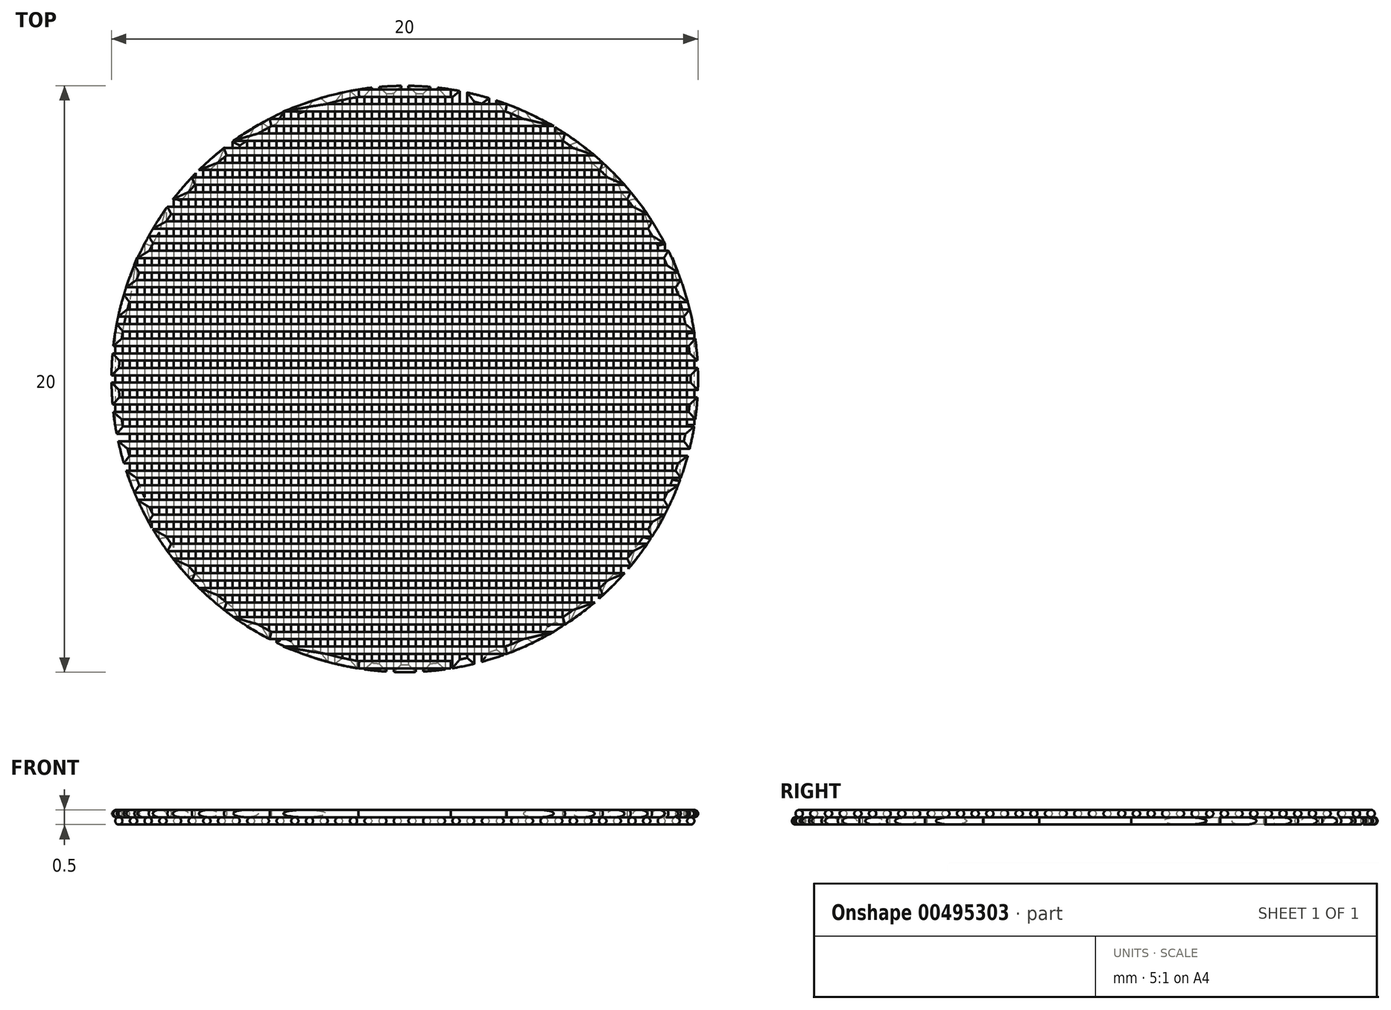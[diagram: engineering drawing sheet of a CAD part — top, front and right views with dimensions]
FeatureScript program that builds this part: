
annotation { "Feature Type Name" : "Feature", "Feature Type Description" : "" }
export const myFeature = defineFeature(function(context is Context, id is Id, definition is map)
    precondition{}
    {
        {
            assignVariable(context, id + "F0", {"name" : "d", "anyValue" : 0.25 * mm});
        }
        {
            var Q0;
            Q0=qCreatedBy(makeId("Top.planeOp"),FACE);
            cPlane(context, id + "F1", {"entities" : qUnion([Q0]), "cplaneType" : CPlaneType.OFFSET, "offset" : getVariable(context, 'd') / 2, "width" : 150 * mm, "height" : 150 * mm});
        }
        {
            var Q0;
            Q0=qCreatedBy(id+"F1.planeOp",FACE);
            var sketch = newSketch(context, id + "F2", { "sketchPlane" : qUnion([Q0])});
            skCircle(sketch, "E0", {"center": v(0, 0) * mm, "radius": 10 * mm, "construction": true});
            skCircle(sketch, "E1", {"center": v(0, 0) * mm, "radius": 9.88 * mm, "construction": true});
            skLineSegment(sketch, "E2", {"start": v(-9.88, 0) * mm, "end": v(-9.75, 0) * mm, "construction": true});
            skLineSegment(sketch, "E3", {"start": v(-9.75, 0) * mm, "end": v(-9.25, 0) * mm, "construction": true});
            skLineSegment(sketch, "E4", {"start": v(-9.25, 0) * mm, "end": v(-8.75, 0) * mm, "construction": true});
            skLineSegment(sketch, "E5", {"start": v(-8.75, 0) * mm, "end": v(-8.25, 0) * mm, "construction": true});
            skLineSegment(sketch, "E6", {"start": v(-8.25, 0) * mm, "end": v(-7.75, 0) * mm, "construction": true});
            skLineSegment(sketch, "E7", {"start": v(-7.75, 0) * mm, "end": v(-7.25, 0) * mm, "construction": true});
            skLineSegment(sketch, "E8", {"start": v(-7.25, 0) * mm, "end": v(-6.75, 0) * mm, "construction": true});
            skLineSegment(sketch, "E9", {"start": v(-6.75, 0) * mm, "end": v(-6.25, 0) * mm, "construction": true});
            skLineSegment(sketch, "E10", {"start": v(-6.25, 0) * mm, "end": v(-5.75, 0) * mm, "construction": true});
            skLineSegment(sketch, "E11", {"start": v(-5.75, 0) * mm, "end": v(-5.25, 0) * mm, "construction": true});
            skLineSegment(sketch, "E12", {"start": v(-5.25, 0) * mm, "end": v(-4.75, 0) * mm, "construction": true});
            skLineSegment(sketch, "E13", {"start": v(-4.75, 0) * mm, "end": v(-4.25, 0) * mm, "construction": true});
            skLineSegment(sketch, "E14", {"start": v(-4.25, 0) * mm, "end": v(-3.75, 0) * mm, "construction": true});
            skLineSegment(sketch, "E15", {"start": v(-3.75, 0) * mm, "end": v(-3.25, 0) * mm, "construction": true});
            skLineSegment(sketch, "E16", {"start": v(-3.25, 0) * mm, "end": v(-2.75, 0) * mm, "construction": true});
            skLineSegment(sketch, "E17", {"start": v(-2.75, 0) * mm, "end": v(-2.25, 0) * mm, "construction": true});
            skLineSegment(sketch, "E18", {"start": v(-2.25, 0) * mm, "end": v(-1.75, 0) * mm, "construction": true});
            skLineSegment(sketch, "E19", {"start": v(-1.75, 0) * mm, "end": v(-1.25, 0) * mm, "construction": true});
            skLineSegment(sketch, "E20", {"start": v(-1.25, 0) * mm, "end": v(-0.75, 0) * mm, "construction": true});
            skLineSegment(sketch, "E21", {"start": v(-0.75, 0) * mm, "end": v(-0.25, 0) * mm, "construction": true});
            skLineSegment(sketch, "E22", {"start": v(-0.25, 0) * mm, "end": v(0.25, 0) * mm, "construction": true});
            skLineSegment(sketch, "E23", {"start": v(0.25, 0) * mm, "end": v(0.75, 0) * mm, "construction": true});
            skLineSegment(sketch, "E24", {"start": v(0.75, 0) * mm, "end": v(1.25, 0) * mm, "construction": true});
            skLineSegment(sketch, "E25", {"start": v(1.25, 0) * mm, "end": v(1.75, 0) * mm, "construction": true});
            skLineSegment(sketch, "E26", {"start": v(1.75, 0) * mm, "end": v(2.25, 0) * mm, "construction": true});
            skLineSegment(sketch, "E27", {"start": v(2.25, 0) * mm, "end": v(2.75, 0) * mm, "construction": true});
            skLineSegment(sketch, "E28", {"start": v(2.75, 0) * mm, "end": v(3.25, 0) * mm, "construction": true});
            skLineSegment(sketch, "E29", {"start": v(3.25, 0) * mm, "end": v(3.75, 0) * mm, "construction": true});
            skLineSegment(sketch, "E30", {"start": v(3.75, 0) * mm, "end": v(4.25, 0) * mm, "construction": true});
            skLineSegment(sketch, "E31", {"start": v(4.25, 0) * mm, "end": v(4.75, 0) * mm, "construction": true});
            skLineSegment(sketch, "E32", {"start": v(4.75, 0) * mm, "end": v(5.25, 0) * mm, "construction": true});
            skLineSegment(sketch, "E33", {"start": v(5.25, 0) * mm, "end": v(5.75, 0) * mm, "construction": true});
            skLineSegment(sketch, "E34", {"start": v(5.75, 0) * mm, "end": v(6.25, 0) * mm, "construction": true});
            skLineSegment(sketch, "E35", {"start": v(6.25, 0) * mm, "end": v(6.75, 0) * mm, "construction": true});
            skLineSegment(sketch, "E36", {"start": v(6.75, 0) * mm, "end": v(7.25, 0) * mm, "construction": true});
            skLineSegment(sketch, "E37", {"start": v(7.25, 0) * mm, "end": v(7.75, 0) * mm, "construction": true});
            skLineSegment(sketch, "E38", {"start": v(7.75, 0) * mm, "end": v(8.25, 0) * mm, "construction": true});
            skLineSegment(sketch, "E39", {"start": v(8.25, 0) * mm, "end": v(8.75, 0) * mm, "construction": true});
            skLineSegment(sketch, "E40", {"start": v(8.75, 0) * mm, "end": v(9.25, 0) * mm, "construction": true});
            skLineSegment(sketch, "E41", {"start": v(9.25, 0) * mm, "end": v(9.75, 0) * mm, "construction": true});
            skLineSegment(sketch, "E42", {"start": v(9.75, 0) * mm, "end": v(9.88, 0) * mm, "construction": true});
            skLineSegment(sketch, "E43", {"start": v(0, 9.88) * mm, "end": v(0, 9.75) * mm, "construction": true});
            skLineSegment(sketch, "E44", {"start": v(0, 9.75) * mm, "end": v(0, 9.25) * mm, "construction": true});
            skLineSegment(sketch, "E45", {"start": v(0, 9.25) * mm, "end": v(0, 8.75) * mm, "construction": true});
            skLineSegment(sketch, "E46", {"start": v(0, 8.75) * mm, "end": v(0, 8.25) * mm, "construction": true});
            skLineSegment(sketch, "E47", {"start": v(0, 8.25) * mm, "end": v(0, 7.75) * mm, "construction": true});
            skLineSegment(sketch, "E48", {"start": v(0, 7.75) * mm, "end": v(0, 7.25) * mm, "construction": true});
            skLineSegment(sketch, "E49", {"start": v(0, 7.25) * mm, "end": v(0, 6.75) * mm, "construction": true});
            skLineSegment(sketch, "E50", {"start": v(0, 6.75) * mm, "end": v(0, 6.25) * mm, "construction": true});
            skLineSegment(sketch, "E51", {"start": v(0, 6.25) * mm, "end": v(0, 5.75) * mm, "construction": true});
            skLineSegment(sketch, "E52", {"start": v(0, 5.75) * mm, "end": v(0, 5.25) * mm, "construction": true});
            skLineSegment(sketch, "E53", {"start": v(0, 5.25) * mm, "end": v(0, 4.75) * mm, "construction": true});
            skLineSegment(sketch, "E54", {"start": v(0, 4.75) * mm, "end": v(0, 4.25) * mm, "construction": true});
            skLineSegment(sketch, "E55", {"start": v(0, 4.25) * mm, "end": v(0, 3.75) * mm, "construction": true});
            skLineSegment(sketch, "E56", {"start": v(0, 3.75) * mm, "end": v(0, 3.25) * mm, "construction": true});
            skLineSegment(sketch, "E57", {"start": v(0, 3.25) * mm, "end": v(0, 2.75) * mm, "construction": true});
            skLineSegment(sketch, "E58", {"start": v(0, 2.75) * mm, "end": v(0, 2.25) * mm, "construction": true});
            skLineSegment(sketch, "E59", {"start": v(0, 2.25) * mm, "end": v(0, 1.75) * mm, "construction": true});
            skLineSegment(sketch, "E60", {"start": v(0, 1.75) * mm, "end": v(0, 1.25) * mm, "construction": true});
            skLineSegment(sketch, "E61", {"start": v(0, 1.25) * mm, "end": v(0, 0.75) * mm, "construction": true});
            skLineSegment(sketch, "E62", {"start": v(0, 0.75) * mm, "end": v(0, 0.25) * mm, "construction": true});
            skLineSegment(sketch, "E63", {"start": v(0, 0.25) * mm, "end": v(0, -0.25) * mm, "construction": true});
            skLineSegment(sketch, "E64", {"start": v(0, -0.25) * mm, "end": v(0, -0.75) * mm, "construction": true});
            skLineSegment(sketch, "E65", {"start": v(0, -0.75) * mm, "end": v(0, -1.25) * mm, "construction": true});
            skLineSegment(sketch, "E66", {"start": v(0, -1.25) * mm, "end": v(0, -1.75) * mm, "construction": true});
            skLineSegment(sketch, "E67", {"start": v(0, -1.75) * mm, "end": v(0, -2.25) * mm, "construction": true});
            skLineSegment(sketch, "E68", {"start": v(0, -2.25) * mm, "end": v(0, -2.75) * mm, "construction": true});
            skLineSegment(sketch, "E69", {"start": v(0, -2.75) * mm, "end": v(0, -3.25) * mm, "construction": true});
            skLineSegment(sketch, "E70", {"start": v(0, -3.25) * mm, "end": v(0, -3.75) * mm, "construction": true});
            skLineSegment(sketch, "E71", {"start": v(0, -3.75) * mm, "end": v(0, -4.25) * mm, "construction": true});
            skLineSegment(sketch, "E72", {"start": v(0, -4.25) * mm, "end": v(0, -4.75) * mm, "construction": true});
            skLineSegment(sketch, "E73", {"start": v(0, -4.75) * mm, "end": v(0, -5.25) * mm, "construction": true});
            skLineSegment(sketch, "E74", {"start": v(0, -5.25) * mm, "end": v(0, -5.75) * mm, "construction": true});
            skLineSegment(sketch, "E75", {"start": v(0, -5.75) * mm, "end": v(0, -6.25) * mm, "construction": true});
            skLineSegment(sketch, "E76", {"start": v(0, -6.25) * mm, "end": v(0, -6.75) * mm, "construction": true});
            skLineSegment(sketch, "E77", {"start": v(0, -6.75) * mm, "end": v(0, -7.25) * mm, "construction": true});
            skLineSegment(sketch, "E78", {"start": v(0, -7.25) * mm, "end": v(0, -7.75) * mm, "construction": true});
            skLineSegment(sketch, "E79", {"start": v(0, -7.75) * mm, "end": v(0, -8.25) * mm, "construction": true});
            skLineSegment(sketch, "E80", {"start": v(0, -8.25) * mm, "end": v(0, -8.75) * mm, "construction": true});
            skLineSegment(sketch, "E81", {"start": v(0, -8.75) * mm, "end": v(0, -9.25) * mm, "construction": true});
            skLineSegment(sketch, "E82", {"start": v(0, -9.25) * mm, "end": v(0, -9.75) * mm, "construction": true});
            skLineSegment(sketch, "E83", {"start": v(0, -9.75) * mm, "end": v(0, -9.88) * mm, "construction": true});
            skLineSegment(sketch, "E84", {"start": v(-9.75, 1.57) * mm, "end": v(-9.75, -1.57) * mm});
            skLineSegment(sketch, "E85", {"start": v(-9.25, 3.46) * mm, "end": v(-9.25, -3.46) * mm});
            skLineSegment(sketch, "E86", {"start": v(-8.75, 4.58) * mm, "end": v(-8.75, -4.58) * mm});
            skLineSegment(sketch, "E87", {"start": v(-8.25, 5.43) * mm, "end": v(-8.25, -5.43) * mm});
            skLineSegment(sketch, "E88", {"start": v(-7.75, 6.12) * mm, "end": v(-7.75, -6.12) * mm});
            skLineSegment(sketch, "E89", {"start": v(-7.25, 6.7) * mm, "end": v(-7.25, -6.7) * mm});
            skLineSegment(sketch, "E90", {"start": v(-6.75, 7.2) * mm, "end": v(-6.75, -7.2) * mm});
            skLineSegment(sketch, "E91", {"start": v(-6.25, 7.65) * mm, "end": v(-6.25, -7.65) * mm});
            skLineSegment(sketch, "E92", {"start": v(-5.75, 8.03) * mm, "end": v(-5.75, -8.03) * mm});
            skLineSegment(sketch, "E93", {"start": v(-5.25, 8.36) * mm, "end": v(-5.25, -8.36) * mm});
            skLineSegment(sketch, "E94", {"start": v(-4.75, 8.66) * mm, "end": v(-4.75, -8.66) * mm});
            skLineSegment(sketch, "E95", {"start": v(-4.25, 8.91) * mm, "end": v(-4.25, -8.91) * mm});
            skLineSegment(sketch, "E96", {"start": v(-3.75, 9.14) * mm, "end": v(-3.75, -9.14) * mm});
            skLineSegment(sketch, "E97", {"start": v(-3.25, 9.32) * mm, "end": v(-3.25, -9.32) * mm});
            skLineSegment(sketch, "E98", {"start": v(-2.75, 9.48) * mm, "end": v(-2.75, -9.48) * mm});
            skLineSegment(sketch, "E99", {"start": v(-2.25, 9.62) * mm, "end": v(-2.25, -9.62) * mm});
            skLineSegment(sketch, "E100", {"start": v(-1.75, -9.72) * mm, "end": v(-1.75, 9.72) * mm});
            skLineSegment(sketch, "E101", {"start": v(-1.25, 9.8) * mm, "end": v(-1.25, -9.8) * mm});
            skLineSegment(sketch, "E102", {"start": v(-0.75, 9.85) * mm, "end": v(-0.75, -9.85) * mm});
            skLineSegment(sketch, "E103", {"start": v(-0.25, 9.87) * mm, "end": v(-0.25, -9.87) * mm});
            skLineSegment(sketch, "E104", {"start": v(0.25, -9.87) * mm, "end": v(0.25, 9.87) * mm});
            skLineSegment(sketch, "E105", {"start": v(0.75, 9.85) * mm, "end": v(0.75, -9.85) * mm});
            skLineSegment(sketch, "E106", {"start": v(1.25, -9.8) * mm, "end": v(1.25, 9.8) * mm});
            skLineSegment(sketch, "E107", {"start": v(1.75, 9.72) * mm, "end": v(1.75, -9.72) * mm});
            skLineSegment(sketch, "E108", {"start": v(2.25, 9.62) * mm, "end": v(2.25, -9.62) * mm});
            skLineSegment(sketch, "E109", {"start": v(2.75, 9.48) * mm, "end": v(2.75, -9.48) * mm});
            skLineSegment(sketch, "E110", {"start": v(3.25, 9.32) * mm, "end": v(3.25, -9.32) * mm});
            skLineSegment(sketch, "E111", {"start": v(3.75, 9.14) * mm, "end": v(3.75, -9.14) * mm});
            skLineSegment(sketch, "E112", {"start": v(4.25, 8.91) * mm, "end": v(4.25, -8.91) * mm});
            skLineSegment(sketch, "E113", {"start": v(4.75, 8.66) * mm, "end": v(4.75, -8.66) * mm});
            skLineSegment(sketch, "E114", {"start": v(5.25, 8.36) * mm, "end": v(5.25, -8.36) * mm});
            skLineSegment(sketch, "E115", {"start": v(5.75, 8.03) * mm, "end": v(5.75, -8.03) * mm});
            skLineSegment(sketch, "E116", {"start": v(6.25, 7.65) * mm, "end": v(6.25, -7.65) * mm});
            skLineSegment(sketch, "E117", {"start": v(6.75, -7.2) * mm, "end": v(6.75, 7.2) * mm});
            skLineSegment(sketch, "E118", {"start": v(7.25, -6.7) * mm, "end": v(7.25, 6.7) * mm});
            skLineSegment(sketch, "E119", {"start": v(7.75, -6.12) * mm, "end": v(7.75, 6.12) * mm});
            skLineSegment(sketch, "E120", {"start": v(8.25, -5.43) * mm, "end": v(8.25, 5.43) * mm});
            skLineSegment(sketch, "E121", {"start": v(8.75, -4.58) * mm, "end": v(8.75, 4.58) * mm});
            skLineSegment(sketch, "E122", {"start": v(9.25, -3.46) * mm, "end": v(9.25, 3.46) * mm});
            skLineSegment(sketch, "E123", {"start": v(9.75, -1.57) * mm, "end": v(9.75, 1.57) * mm});
            skArc(sketch, "E124", {"start": v(9.75, 1.57) * mm, "mid": v(9.55, 2.52) * mm, "end": v(9.25, 3.46) * mm});
            skArc(sketch, "E125", {"start": v(8.75, 4.58) * mm, "mid": v(8.51, 5) * mm, "end": v(8.25, 5.43) * mm});
            skArc(sketch, "E126", {"start": v(7.75, 6.12) * mm, "mid": v(7.5, 6.42) * mm, "end": v(7.25, 6.7) * mm});
            skArc(sketch, "E127", {"start": v(6.75, 7.2) * mm, "mid": v(6.5, 7.43) * mm, "end": v(6.25, 7.65) * mm});
            skArc(sketch, "E128", {"start": v(5.75, 8.03) * mm, "mid": v(5.5, 8.2) * mm, "end": v(5.25, 8.36) * mm});
            skArc(sketch, "E129", {"start": v(4.75, 8.66) * mm, "mid": v(4.5, 8.79) * mm, "end": v(4.25, 8.91) * mm});
            skArc(sketch, "E130", {"start": v(3.75, 9.14) * mm, "mid": v(3.5, 9.23) * mm, "end": v(3.25, 9.32) * mm});
            skArc(sketch, "E131", {"start": v(2.75, 9.48) * mm, "mid": v(2.5, 9.55) * mm, "end": v(2.25, 9.62) * mm});
            skArc(sketch, "E132", {"start": v(1.75, 9.72) * mm, "mid": v(1.5, 9.76) * mm, "end": v(1.25, 9.8) * mm});
            skArc(sketch, "E133", {"start": v(0.75, 9.85) * mm, "mid": v(0.5, 9.86) * mm, "end": v(0.25, 9.87) * mm});
            skArc(sketch, "E134", {"start": v(-0.25, 9.87) * mm, "mid": v(-0.5, 9.86) * mm, "end": v(-0.75, 9.85) * mm});
            skArc(sketch, "E135", {"start": v(-1.25, 9.8) * mm, "mid": v(-1.5, 9.76) * mm, "end": v(-1.75, 9.72) * mm});
            skArc(sketch, "E136", {"start": v(-2.25, 9.62) * mm, "mid": v(-2.5, 9.55) * mm, "end": v(-2.75, 9.48) * mm});
            skArc(sketch, "E137", {"start": v(-3.25, 9.32) * mm, "mid": v(-3.5, 9.23) * mm, "end": v(-3.75, 9.14) * mm});
            skArc(sketch, "E138", {"start": v(-4.25, 8.91) * mm, "mid": v(-4.5, 8.79) * mm, "end": v(-4.75, 8.66) * mm});
            skArc(sketch, "E139", {"start": v(-5.25, 8.36) * mm, "mid": v(-5.5, 8.2) * mm, "end": v(-5.75, 8.03) * mm});
            skArc(sketch, "E140", {"start": v(-6.25, 7.65) * mm, "mid": v(-6.5, 7.43) * mm, "end": v(-6.75, 7.2) * mm});
            skArc(sketch, "E141", {"start": v(-7.25, 6.7) * mm, "mid": v(-7.5, 6.42) * mm, "end": v(-7.75, 6.12) * mm});
            skArc(sketch, "E142", {"start": v(-8.25, 5.43) * mm, "mid": v(-8.51, 5) * mm, "end": v(-8.75, 4.58) * mm});
            skArc(sketch, "E143", {"start": v(-9.25, 3.46) * mm, "mid": v(-9.55, 2.52) * mm, "end": v(-9.75, 1.57) * mm});
            skArc(sketch, "E144", {"start": v(-9.25, -3.46) * mm, "mid": v(-9.02, -4.03) * mm, "end": v(-8.75, -4.58) * mm});
            skArc(sketch, "E145", {"start": v(-8.25, -5.43) * mm, "mid": v(-8, -5.78) * mm, "end": v(-7.75, -6.12) * mm});
            skArc(sketch, "E146", {"start": v(-7.25, -6.7) * mm, "mid": v(-7, -6.96) * mm, "end": v(-6.75, -7.2) * mm});
            skArc(sketch, "E147", {"start": v(-6.25, -7.65) * mm, "mid": v(-6, -7.84) * mm, "end": v(-5.75, -8.03) * mm});
            skArc(sketch, "E148", {"start": v(-5.25, -8.36) * mm, "mid": v(-5, -8.51) * mm, "end": v(-4.75, -8.66) * mm});
            skArc(sketch, "E149", {"start": v(-4.25, -8.91) * mm, "mid": v(-4, -9.03) * mm, "end": v(-3.75, -9.14) * mm});
            skArc(sketch, "E150", {"start": v(-3.25, -9.32) * mm, "mid": v(-3, -9.4) * mm, "end": v(-2.75, -9.48) * mm});
            skArc(sketch, "E151", {"start": v(-2.25, -9.62) * mm, "mid": v(-2, -9.67) * mm, "end": v(-1.75, -9.72) * mm});
            skArc(sketch, "E152", {"start": v(-1.25, -9.8) * mm, "mid": v(-1, -9.82) * mm, "end": v(-0.75, -9.85) * mm});
            skArc(sketch, "E153", {"start": v(-0.25, -9.87) * mm, "mid": v(0, -9.88) * mm, "end": v(0.25, -9.87) * mm});
            skArc(sketch, "E154", {"start": v(0.75, -9.85) * mm, "mid": v(1, -9.82) * mm, "end": v(1.25, -9.8) * mm});
            skArc(sketch, "E155", {"start": v(1.75, -9.72) * mm, "mid": v(2, -9.67) * mm, "end": v(2.25, -9.62) * mm});
            skArc(sketch, "E156", {"start": v(2.75, -9.48) * mm, "mid": v(3, -9.4) * mm, "end": v(3.25, -9.32) * mm});
            skArc(sketch, "E157", {"start": v(3.75, -9.14) * mm, "mid": v(4, -9.03) * mm, "end": v(4.25, -8.91) * mm});
            skArc(sketch, "E158", {"start": v(4.75, -8.66) * mm, "mid": v(5, -8.51) * mm, "end": v(5.25, -8.36) * mm});
            skArc(sketch, "E159", {"start": v(5.75, -8.03) * mm, "mid": v(6, -7.84) * mm, "end": v(6.25, -7.65) * mm});
            skArc(sketch, "E160", {"start": v(6.75, -7.2) * mm, "mid": v(7, -6.96) * mm, "end": v(7.25, -6.7) * mm});
            skArc(sketch, "E161", {"start": v(7.75, -6.12) * mm, "mid": v(8, -5.78) * mm, "end": v(8.25, -5.43) * mm});
            skArc(sketch, "E162", {"start": v(8.75, -4.58) * mm, "mid": v(9.02, -4.03) * mm, "end": v(9.25, -3.46) * mm});
            skSolve(sketch);
        }
        {
            var Q0;
            Q0=sQuery(id+"F2.wireOp",EDGE,"E123");
            var Q1;
            Q1=sQuery(id+"F2.wireOp",VERTEX,"E123.start");
            cPlane(context, id + "F3", {"entities" : qUnion([Q0, Q1]), "cplaneType" : CPlaneType.LINE_POINT, "offset" : 25 * mm, "width" : 150 * mm, "height" : 150 * mm});
        }
        {
            var Q0;
            Q0=qCreatedBy(id+"F3.planeOp",FACE);
            var sketch = newSketch(context, id + "F4", { "sketchPlane" : qUnion([Q0])});
            skCircle(sketch, "E163", {"center": v(-9.75, 0.12) * mm, "radius": 0.12 * mm});
            skSolve(sketch);
        }
        {
            var Q0;
            Q0=makeQuery(id+"F4.imprint","IMPRINT",FACE,{"disambiguationData":[TD([[makeQuery(id+"F4.imprint","IMPRINT",EDGE,{"derivedFrom":sQuery(id+"F4.wireOp",EDGE,"E163")}),1.0]])]});
            var Q1;
            Q1=sQuery(id+"F2.wireOp",EDGE,"E123");
            var Q2;
            Q2=sQuery(id+"F2.wireOp",EDGE,"E124");
            var Q3;
            Q3=sQuery(id+"F2.wireOp",EDGE,"E122");
            var Q4;
            Q4=sQuery(id+"F2.wireOp",EDGE,"E162");
            var Q5;
            Q5=sQuery(id+"F2.wireOp",EDGE,"E120");
            var Q6;
            Q6=sQuery(id+"F2.wireOp",EDGE,"E125");
            var Q7;
            Q7=sQuery(id+"F2.wireOp",EDGE,"E121");
            var Q8;
            Q8=sQuery(id+"F2.wireOp",EDGE,"E126");
            var Q9;
            Q9=sQuery(id+"F2.wireOp",EDGE,"E119");
            var Q10;
            Q10=sQuery(id+"F2.wireOp",EDGE,"E118");
            var Q11;
            Q11=sQuery(id+"F2.wireOp",EDGE,"E117");
            var Q12;
            Q12=sQuery(id+"F2.wireOp",EDGE,"E127");
            var Q13;
            Q13=sQuery(id+"F2.wireOp",EDGE,"E116");
            var Q14;
            Q14=sQuery(id+"F2.wireOp",EDGE,"E115");
            var Q15;
            Q15=sQuery(id+"F2.wireOp",EDGE,"E128");
            var Q16;
            Q16=sQuery(id+"F2.wireOp",EDGE,"E114");
            var Q17;
            Q17=sQuery(id+"F2.wireOp",EDGE,"E113");
            var Q18;
            Q18=sQuery(id+"F2.wireOp",EDGE,"E112");
            var Q19;
            Q19=sQuery(id+"F2.wireOp",EDGE,"E111");
            var Q20;
            Q20=sQuery(id+"F2.wireOp",EDGE,"E110");
            var Q21;
            Q21=sQuery(id+"F2.wireOp",EDGE,"E109");
            var Q22;
            Q22=sQuery(id+"F2.wireOp",EDGE,"E129");
            var Q23;
            Q23=sQuery(id+"F2.wireOp",EDGE,"E130");
            var Q24;
            Q24=sQuery(id+"F2.wireOp",EDGE,"E131");
            var Q25;
            Q25=sQuery(id+"F2.wireOp",EDGE,"E108");
            var Q26;
            Q26=sQuery(id+"F2.wireOp",EDGE,"E107");
            var Q27;
            Q27=sQuery(id+"F2.wireOp",EDGE,"E132");
            var Q28;
            Q28=sQuery(id+"F2.wireOp",EDGE,"E106");
            var Q29;
            Q29=sQuery(id+"F2.wireOp",EDGE,"E133");
            var Q30;
            Q30=sQuery(id+"F2.wireOp",EDGE,"E105");
            var Q31;
            Q31=sQuery(id+"F2.wireOp",EDGE,"E104");
            var Q32;
            Q32=sQuery(id+"F2.wireOp",EDGE,"E134");
            var Q33;
            Q33=sQuery(id+"F2.wireOp",EDGE,"E101");
            var Q34;
            Q34=sQuery(id+"F2.wireOp",EDGE,"E135");
            var Q35;
            Q35=sQuery(id+"F2.wireOp",EDGE,"E100");
            var Q36;
            Q36=sQuery(id+"F2.wireOp",EDGE,"E99");
            var Q37;
            Q37=sQuery(id+"F2.wireOp",EDGE,"E136");
            var Q38;
            Q38=sQuery(id+"F2.wireOp",EDGE,"E98");
            var Q39;
            Q39=sQuery(id+"F2.wireOp",EDGE,"E97");
            var Q40;
            Q40=sQuery(id+"F2.wireOp",EDGE,"E137");
            var Q41;
            Q41=sQuery(id+"F2.wireOp",EDGE,"E96");
            var Q42;
            Q42=sQuery(id+"F2.wireOp",EDGE,"E95");
            var Q43;
            Q43=sQuery(id+"F2.wireOp",EDGE,"E138");
            var Q44;
            Q44=sQuery(id+"F2.wireOp",EDGE,"E94");
            var Q45;
            Q45=sQuery(id+"F2.wireOp",EDGE,"E93");
            var Q46;
            Q46=sQuery(id+"F2.wireOp",EDGE,"E139");
            var Q47;
            Q47=sQuery(id+"F2.wireOp",EDGE,"E92");
            var Q48;
            Q48=sQuery(id+"F2.wireOp",EDGE,"E91");
            var Q49;
            Q49=sQuery(id+"F2.wireOp",EDGE,"E140");
            var Q50;
            Q50=sQuery(id+"F2.wireOp",EDGE,"E90");
            var Q51;
            Q51=sQuery(id+"F2.wireOp",EDGE,"E89");
            var Q52;
            Q52=sQuery(id+"F2.wireOp",EDGE,"E141");
            var Q53;
            Q53=sQuery(id+"F2.wireOp",EDGE,"E88");
            var Q54;
            Q54=sQuery(id+"F2.wireOp",EDGE,"E102");
            var Q55;
            Q55=sQuery(id+"F2.wireOp",EDGE,"E103");
            var Q56;
            Q56=sQuery(id+"F2.wireOp",EDGE,"E87");
            var Q57;
            Q57=sQuery(id+"F2.wireOp",EDGE,"E142");
            var Q58;
            Q58=sQuery(id+"F2.wireOp",EDGE,"E86");
            var Q59;
            Q59=sQuery(id+"F2.wireOp",EDGE,"E85");
            var Q60;
            Q60=sQuery(id+"F2.wireOp",EDGE,"E143");
            var Q61;
            Q61=sQuery(id+"F2.wireOp",EDGE,"E84");
            var Q62;
            Q62=sQuery(id+"F2.wireOp",EDGE,"E144");
            var Q63;
            Q63=sQuery(id+"F2.wireOp",EDGE,"E145");
            var Q64;
            Q64=sQuery(id+"F2.wireOp",EDGE,"E146");
            var Q65;
            Q65=sQuery(id+"F2.wireOp",EDGE,"E147");
            var Q66;
            Q66=sQuery(id+"F2.wireOp",EDGE,"E148");
            var Q67;
            Q67=sQuery(id+"F2.wireOp",EDGE,"E149");
            var Q68;
            Q68=sQuery(id+"F2.wireOp",EDGE,"E150");
            var Q69;
            Q69=sQuery(id+"F2.wireOp",EDGE,"E151");
            var Q70;
            Q70=sQuery(id+"F2.wireOp",EDGE,"E152");
            var Q71;
            Q71=sQuery(id+"F2.wireOp",EDGE,"E153");
            var Q72;
            Q72=sQuery(id+"F2.wireOp",EDGE,"E154");
            var Q73;
            Q73=sQuery(id+"F2.wireOp",EDGE,"E155");
            var Q74;
            Q74=sQuery(id+"F2.wireOp",EDGE,"E156");
            var Q75;
            Q75=sQuery(id+"F2.wireOp",EDGE,"E157");
            var Q76;
            Q76=sQuery(id+"F2.wireOp",EDGE,"E158");
            var Q77;
            Q77=sQuery(id+"F2.wireOp",EDGE,"E159");
            var Q78;
            Q78=sQuery(id+"F2.wireOp",EDGE,"E160");
            var Q79;
            Q79=sQuery(id+"F2.wireOp",EDGE,"E161");
            var Q80;
            Q80=sQuery(id+"F2.wireOp",EDGE,"E146");
            var Q81;
            Q81=sQuery(id+"F2.wireOp",EDGE,"E147");
            var Q82;
            Q82=sQuery(id+"F2.wireOp",EDGE,"E157");
            sweep(context, id + "F5", {"profiles" : qUnion([Q0]), "path" : qUnion([Q1, Q2, Q3, Q4, Q5, Q6, Q7, Q8, Q9, Q10, Q11, Q12, Q13, Q14, Q15, Q16, Q17, Q18, Q19, Q20, Q21, Q22, Q23, Q24, Q25, Q26, Q27, Q28, Q29, Q30, Q31, Q32, Q33, Q34, Q35, Q36, Q37, Q38, Q39, Q40, Q41, Q42, Q43, Q44, Q45, Q46, Q47, Q48, Q49, Q50, Q51, Q52, Q53, Q54, Q55, Q56, Q57, Q58, Q59, Q60, Q61, Q62, Q63, Q64, Q65, Q66, Q67, Q68, Q69, Q70, Q71, Q72, Q73, Q74, Q75, Q76, Q77, Q78, Q79, Q80, Q81, Q82])});
        }
        {
            var Q0;
            Q0=qCreatedBy(id+"F1.planeOp",FACE);
            cPlane(context, id + "F6", {"entities" : qUnion([Q0]), "cplaneType" : CPlaneType.OFFSET, "offset" : getVariable(context, 'd'), "width" : 150 * mm, "height" : 150 * mm});
        }
        {
            var Q0;
            Q0=qCreatedBy(id+"F6.planeOp",FACE);
            var sketch = newSketch(context, id + "F7", { "sketchPlane" : qUnion([Q0])});
            skCircle(sketch, "E164", {"center": v(0, 0) * mm, "radius": 10 * mm, "construction": true});
            skCircle(sketch, "E165", {"center": v(0, 0) * mm, "radius": 9.88 * mm, "construction": true});
            skLineSegment(sketch, "E166", {"start": v(0, -9.88) * mm, "end": v(0, -9.75) * mm, "construction": true});
            skLineSegment(sketch, "E167", {"start": v(0, -9.75) * mm, "end": v(0, -9.25) * mm, "construction": true});
            skLineSegment(sketch, "E168", {"start": v(0, -9.25) * mm, "end": v(0, -8.75) * mm, "construction": true});
            skLineSegment(sketch, "E169", {"start": v(0, -8.75) * mm, "end": v(0, -8.25) * mm, "construction": true});
            skLineSegment(sketch, "E170", {"start": v(0, -8.25) * mm, "end": v(0, -7.75) * mm, "construction": true});
            skLineSegment(sketch, "E171", {"start": v(0, -7.75) * mm, "end": v(0, -7.25) * mm, "construction": true});
            skLineSegment(sketch, "E172", {"start": v(0, -7.25) * mm, "end": v(0, -6.75) * mm, "construction": true});
            skLineSegment(sketch, "E173", {"start": v(0, -6.75) * mm, "end": v(0, -6.25) * mm, "construction": true});
            skLineSegment(sketch, "E174", {"start": v(0, -6.25) * mm, "end": v(0, -5.75) * mm, "construction": true});
            skLineSegment(sketch, "E175", {"start": v(0, -5.75) * mm, "end": v(0, -5.25) * mm, "construction": true});
            skLineSegment(sketch, "E176", {"start": v(0, -5.25) * mm, "end": v(0, -4.75) * mm, "construction": true});
            skLineSegment(sketch, "E177", {"start": v(0, -4.75) * mm, "end": v(0, -4.25) * mm, "construction": true});
            skLineSegment(sketch, "E178", {"start": v(0, -4.25) * mm, "end": v(0, -3.75) * mm, "construction": true});
            skLineSegment(sketch, "E179", {"start": v(0, -3.75) * mm, "end": v(0, -3.25) * mm, "construction": true});
            skLineSegment(sketch, "E180", {"start": v(0, -3.25) * mm, "end": v(0, -2.75) * mm, "construction": true});
            skLineSegment(sketch, "E181", {"start": v(0, -2.75) * mm, "end": v(0, -2.25) * mm, "construction": true});
            skLineSegment(sketch, "E182", {"start": v(0, -2.25) * mm, "end": v(0, -1.75) * mm, "construction": true});
            skLineSegment(sketch, "E183", {"start": v(0, -1.75) * mm, "end": v(0, -1.25) * mm, "construction": true});
            skLineSegment(sketch, "E184", {"start": v(0, -1.25) * mm, "end": v(0, -0.75) * mm, "construction": true});
            skLineSegment(sketch, "E185", {"start": v(0, -0.75) * mm, "end": v(0, -0.25) * mm, "construction": true});
            skLineSegment(sketch, "E186", {"start": v(0, -0.25) * mm, "end": v(0, 0.25) * mm, "construction": true});
            skLineSegment(sketch, "E187", {"start": v(0, 0.25) * mm, "end": v(0, 0.75) * mm, "construction": true});
            skLineSegment(sketch, "E188", {"start": v(0, 0.75) * mm, "end": v(0, 1.25) * mm, "construction": true});
            skLineSegment(sketch, "E189", {"start": v(0, 1.25) * mm, "end": v(0, 1.75) * mm, "construction": true});
            skLineSegment(sketch, "E190", {"start": v(0, 1.75) * mm, "end": v(0, 2.25) * mm, "construction": true});
            skLineSegment(sketch, "E191", {"start": v(0, 2.25) * mm, "end": v(0, 2.75) * mm, "construction": true});
            skLineSegment(sketch, "E192", {"start": v(0, 2.75) * mm, "end": v(0, 3.25) * mm, "construction": true});
            skLineSegment(sketch, "E193", {"start": v(0, 3.25) * mm, "end": v(0, 3.75) * mm, "construction": true});
            skLineSegment(sketch, "E194", {"start": v(0, 3.75) * mm, "end": v(0, 4.25) * mm, "construction": true});
            skLineSegment(sketch, "E195", {"start": v(0, 4.25) * mm, "end": v(0, 4.75) * mm, "construction": true});
            skLineSegment(sketch, "E196", {"start": v(0, 4.75) * mm, "end": v(0, 5.25) * mm, "construction": true});
            skLineSegment(sketch, "E197", {"start": v(0, 5.25) * mm, "end": v(0, 5.75) * mm, "construction": true});
            skLineSegment(sketch, "E198", {"start": v(0, 5.75) * mm, "end": v(0, 6.25) * mm, "construction": true});
            skLineSegment(sketch, "E199", {"start": v(0, 6.25) * mm, "end": v(0, 6.75) * mm, "construction": true});
            skLineSegment(sketch, "E200", {"start": v(0, 6.75) * mm, "end": v(0, 7.25) * mm, "construction": true});
            skLineSegment(sketch, "E201", {"start": v(0, 7.25) * mm, "end": v(0, 7.75) * mm, "construction": true});
            skLineSegment(sketch, "E202", {"start": v(0, 7.75) * mm, "end": v(0, 8.25) * mm, "construction": true});
            skLineSegment(sketch, "E203", {"start": v(0, 8.25) * mm, "end": v(0, 8.75) * mm, "construction": true});
            skLineSegment(sketch, "E204", {"start": v(0, 8.75) * mm, "end": v(0, 9.25) * mm, "construction": true});
            skLineSegment(sketch, "E205", {"start": v(0, 9.25) * mm, "end": v(0, 9.75) * mm, "construction": true});
            skLineSegment(sketch, "E206", {"start": v(0, 9.75) * mm, "end": v(0, 9.88) * mm, "construction": true});
            skLineSegment(sketch, "E207", {"start": v(-1.57, -9.75) * mm, "end": v(1.57, -9.75) * mm});
            skLineSegment(sketch, "E208", {"start": v(-3.46, -9.25) * mm, "end": v(3.46, -9.25) * mm});
            skLineSegment(sketch, "E209", {"start": v(-4.58, -8.75) * mm, "end": v(4.58, -8.75) * mm});
            skLineSegment(sketch, "E210", {"start": v(-5.43, -8.25) * mm, "end": v(5.43, -8.25) * mm});
            skLineSegment(sketch, "E211", {"start": v(-6.12, -7.75) * mm, "end": v(6.12, -7.75) * mm});
            skLineSegment(sketch, "E212", {"start": v(-6.7, -7.25) * mm, "end": v(6.7, -7.25) * mm});
            skLineSegment(sketch, "E213", {"start": v(-7.2, -6.75) * mm, "end": v(7.2, -6.75) * mm});
            skLineSegment(sketch, "E214", {"start": v(-7.65, -6.25) * mm, "end": v(7.65, -6.25) * mm});
            skLineSegment(sketch, "E215", {"start": v(-8.03, -5.75) * mm, "end": v(8.03, -5.75) * mm});
            skLineSegment(sketch, "E216", {"start": v(-8.36, -5.25) * mm, "end": v(8.36, -5.25) * mm});
            skLineSegment(sketch, "E217", {"start": v(-8.66, -4.75) * mm, "end": v(8.66, -4.75) * mm});
            skLineSegment(sketch, "E218", {"start": v(-8.91, -4.25) * mm, "end": v(8.91, -4.25) * mm});
            skLineSegment(sketch, "E219", {"start": v(-9.14, -3.75) * mm, "end": v(9.14, -3.75) * mm});
            skLineSegment(sketch, "E220", {"start": v(-9.32, -3.25) * mm, "end": v(9.32, -3.25) * mm});
            skLineSegment(sketch, "E221", {"start": v(-9.48, -2.75) * mm, "end": v(9.48, -2.75) * mm});
            skLineSegment(sketch, "E222", {"start": v(-9.62, -2.25) * mm, "end": v(9.62, -2.25) * mm});
            skLineSegment(sketch, "E223", {"start": v(9.72, -1.75) * mm, "end": v(-9.72, -1.75) * mm});
            skLineSegment(sketch, "E224", {"start": v(-9.8, -1.25) * mm, "end": v(9.8, -1.25) * mm});
            skLineSegment(sketch, "E225", {"start": v(-9.85, -0.75) * mm, "end": v(9.85, -0.75) * mm});
            skLineSegment(sketch, "E226", {"start": v(-9.87, -0.25) * mm, "end": v(9.87, -0.25) * mm});
            skLineSegment(sketch, "E227", {"start": v(9.87, 0.25) * mm, "end": v(-9.87, 0.25) * mm});
            skLineSegment(sketch, "E228", {"start": v(-9.85, 0.75) * mm, "end": v(9.85, 0.75) * mm});
            skLineSegment(sketch, "E229", {"start": v(9.8, 1.25) * mm, "end": v(-9.8, 1.25) * mm});
            skLineSegment(sketch, "E230", {"start": v(-9.72, 1.75) * mm, "end": v(9.72, 1.75) * mm});
            skLineSegment(sketch, "E231", {"start": v(-9.62, 2.25) * mm, "end": v(9.62, 2.25) * mm});
            skLineSegment(sketch, "E232", {"start": v(-9.48, 2.75) * mm, "end": v(9.48, 2.75) * mm});
            skLineSegment(sketch, "E233", {"start": v(-9.32, 3.25) * mm, "end": v(9.32, 3.25) * mm});
            skLineSegment(sketch, "E234", {"start": v(-9.14, 3.75) * mm, "end": v(9.14, 3.75) * mm});
            skLineSegment(sketch, "E235", {"start": v(-8.91, 4.25) * mm, "end": v(8.91, 4.25) * mm});
            skLineSegment(sketch, "E236", {"start": v(-8.66, 4.75) * mm, "end": v(8.66, 4.75) * mm});
            skLineSegment(sketch, "E237", {"start": v(-8.36, 5.25) * mm, "end": v(8.36, 5.25) * mm});
            skLineSegment(sketch, "E238", {"start": v(-8.03, 5.75) * mm, "end": v(8.03, 5.75) * mm});
            skLineSegment(sketch, "E239", {"start": v(-7.65, 6.25) * mm, "end": v(7.65, 6.25) * mm});
            skLineSegment(sketch, "E240", {"start": v(7.2, 6.75) * mm, "end": v(-7.2, 6.75) * mm});
            skLineSegment(sketch, "E241", {"start": v(6.7, 7.25) * mm, "end": v(-6.7, 7.25) * mm});
            skLineSegment(sketch, "E242", {"start": v(6.12, 7.75) * mm, "end": v(-6.12, 7.75) * mm});
            skLineSegment(sketch, "E243", {"start": v(5.43, 8.25) * mm, "end": v(-5.43, 8.25) * mm});
            skLineSegment(sketch, "E244", {"start": v(4.58, 8.75) * mm, "end": v(-4.58, 8.75) * mm});
            skLineSegment(sketch, "E245", {"start": v(3.46, 9.25) * mm, "end": v(-3.46, 9.25) * mm});
            skLineSegment(sketch, "E246", {"start": v(1.57, 9.75) * mm, "end": v(-1.57, 9.75) * mm});
            skArc(sketch, "E247", {"start": v(-1.57, 9.75) * mm, "mid": v(-2.52, 9.55) * mm, "end": v(-3.46, 9.25) * mm});
            skArc(sketch, "E248", {"start": v(-4.58, 8.75) * mm, "mid": v(-5, 8.51) * mm, "end": v(-5.43, 8.25) * mm});
            skArc(sketch, "E249", {"start": v(-6.12, 7.75) * mm, "mid": v(-6.42, 7.5) * mm, "end": v(-6.7, 7.25) * mm});
            skArc(sketch, "E250", {"start": v(-7.2, 6.75) * mm, "mid": v(-7.43, 6.5) * mm, "end": v(-7.65, 6.25) * mm});
            skArc(sketch, "E251", {"start": v(-8.03, 5.75) * mm, "mid": v(-8.2, 5.5) * mm, "end": v(-8.36, 5.25) * mm});
            skArc(sketch, "E252", {"start": v(-8.66, 4.75) * mm, "mid": v(-8.79, 4.5) * mm, "end": v(-8.91, 4.25) * mm});
            skArc(sketch, "E253", {"start": v(-9.14, 3.75) * mm, "mid": v(-9.23, 3.5) * mm, "end": v(-9.32, 3.25) * mm});
            skArc(sketch, "E254", {"start": v(-9.48, 2.75) * mm, "mid": v(-9.55, 2.5) * mm, "end": v(-9.62, 2.25) * mm});
            skArc(sketch, "E255", {"start": v(-9.72, 1.75) * mm, "mid": v(-9.76, 1.5) * mm, "end": v(-9.8, 1.25) * mm});
            skArc(sketch, "E256", {"start": v(-9.85, 0.75) * mm, "mid": v(-9.86, 0.5) * mm, "end": v(-9.87, 0.25) * mm});
            skArc(sketch, "E257", {"start": v(-9.87, -0.25) * mm, "mid": v(-9.86, -0.5) * mm, "end": v(-9.85, -0.75) * mm});
            skArc(sketch, "E258", {"start": v(-9.8, -1.25) * mm, "mid": v(-9.76, -1.5) * mm, "end": v(-9.72, -1.75) * mm});
            skArc(sketch, "E259", {"start": v(-9.62, -2.25) * mm, "mid": v(-9.55, -2.5) * mm, "end": v(-9.48, -2.75) * mm});
            skArc(sketch, "E260", {"start": v(-9.32, -3.25) * mm, "mid": v(-9.23, -3.5) * mm, "end": v(-9.14, -3.75) * mm});
            skArc(sketch, "E261", {"start": v(-8.91, -4.25) * mm, "mid": v(-8.79, -4.5) * mm, "end": v(-8.66, -4.75) * mm});
            skArc(sketch, "E262", {"start": v(-8.36, -5.25) * mm, "mid": v(-8.2, -5.5) * mm, "end": v(-8.03, -5.75) * mm});
            skArc(sketch, "E263", {"start": v(-7.65, -6.25) * mm, "mid": v(-7.43, -6.5) * mm, "end": v(-7.2, -6.75) * mm});
            skArc(sketch, "E264", {"start": v(-6.7, -7.25) * mm, "mid": v(-6.42, -7.5) * mm, "end": v(-6.12, -7.75) * mm});
            skArc(sketch, "E265", {"start": v(-5.43, -8.25) * mm, "mid": v(-5, -8.51) * mm, "end": v(-4.58, -8.75) * mm});
            skArc(sketch, "E266", {"start": v(-3.46, -9.25) * mm, "mid": v(-2.52, -9.55) * mm, "end": v(-1.57, -9.75) * mm});
            skArc(sketch, "E267", {"start": v(3.46, -9.25) * mm, "mid": v(4.03, -9.02) * mm, "end": v(4.58, -8.75) * mm});
            skArc(sketch, "E268", {"start": v(5.43, -8.25) * mm, "mid": v(5.78, -8) * mm, "end": v(6.12, -7.75) * mm});
            skArc(sketch, "E269", {"start": v(6.7, -7.25) * mm, "mid": v(6.96, -7) * mm, "end": v(7.2, -6.75) * mm});
            skArc(sketch, "E270", {"start": v(7.65, -6.25) * mm, "mid": v(7.84, -6) * mm, "end": v(8.03, -5.75) * mm});
            skArc(sketch, "E271", {"start": v(8.36, -5.25) * mm, "mid": v(8.51, -5) * mm, "end": v(8.66, -4.75) * mm});
            skArc(sketch, "E272", {"start": v(8.91, -4.25) * mm, "mid": v(9.03, -4) * mm, "end": v(9.14, -3.75) * mm});
            skArc(sketch, "E273", {"start": v(9.32, -3.25) * mm, "mid": v(9.4, -3) * mm, "end": v(9.48, -2.75) * mm});
            skArc(sketch, "E274", {"start": v(9.62, -2.25) * mm, "mid": v(9.67, -2) * mm, "end": v(9.72, -1.75) * mm});
            skArc(sketch, "E275", {"start": v(9.8, -1.25) * mm, "mid": v(9.82, -1) * mm, "end": v(9.85, -0.75) * mm});
            skArc(sketch, "E276", {"start": v(9.87, -0.25) * mm, "mid": v(9.88, 0) * mm, "end": v(9.87, 0.25) * mm});
            skArc(sketch, "E277", {"start": v(9.85, 0.75) * mm, "mid": v(9.82, 1) * mm, "end": v(9.8, 1.25) * mm});
            skArc(sketch, "E278", {"start": v(9.72, 1.75) * mm, "mid": v(9.67, 2) * mm, "end": v(9.62, 2.25) * mm});
            skArc(sketch, "E279", {"start": v(9.48, 2.75) * mm, "mid": v(9.4, 3) * mm, "end": v(9.32, 3.25) * mm});
            skArc(sketch, "E280", {"start": v(9.14, 3.75) * mm, "mid": v(9.03, 4) * mm, "end": v(8.91, 4.25) * mm});
            skArc(sketch, "E281", {"start": v(8.66, 4.75) * mm, "mid": v(8.51, 5) * mm, "end": v(8.36, 5.25) * mm});
            skArc(sketch, "E282", {"start": v(8.03, 5.75) * mm, "mid": v(7.84, 6) * mm, "end": v(7.65, 6.25) * mm});
            skArc(sketch, "E283", {"start": v(7.2, 6.75) * mm, "mid": v(6.96, 7) * mm, "end": v(6.7, 7.25) * mm});
            skArc(sketch, "E284", {"start": v(6.12, 7.75) * mm, "mid": v(5.78, 8) * mm, "end": v(5.43, 8.25) * mm});
            skArc(sketch, "E285", {"start": v(4.58, 8.75) * mm, "mid": v(4.03, 9.02) * mm, "end": v(3.46, 9.25) * mm});
            skSolve(sketch);
        }
        {
            var Q0;
            Q0=sQuery(id+"F7.wireOp",EDGE,"E246");
            var Q1;
            Q1=sQuery(id+"F7.wireOp",VERTEX,"E246.start");
            cPlane(context, id + "F8", {"entities" : qUnion([Q0, Q1]), "cplaneType" : CPlaneType.LINE_POINT, "offset" : 25 * mm, "width" : 150 * mm, "height" : 150 * mm});
        }
        {
            var Q0;
            Q0=qCreatedBy(id+"F8.planeOp",FACE);
            var sketch = newSketch(context, id + "F9", { "sketchPlane" : qUnion([Q0])});
            skCircle(sketch, "E286", {"center": v(-9.75, 0.38) * mm, "radius": 0.12 * mm});
            skSolve(sketch);
        }
        {
            var Q0;
            Q0=makeQuery(id+"F9.imprint","IMPRINT",FACE,{"disambiguationData":[TD([[makeQuery(id+"F9.imprint","IMPRINT",EDGE,{"derivedFrom":sQuery(id+"F9.wireOp",EDGE,"E286")}),1.0]])]});
            var Q1;
            Q1=sQuery(id+"F7.wireOp",EDGE,"E246");
            var Q2;
            Q2=sQuery(id+"F7.wireOp",EDGE,"E247");
            var Q3;
            Q3=sQuery(id+"F7.wireOp",EDGE,"E245");
            var Q4;
            Q4=sQuery(id+"F7.wireOp",EDGE,"E244");
            var Q5;
            Q5=sQuery(id+"F7.wireOp",EDGE,"E243");
            var Q6;
            Q6=sQuery(id+"F7.wireOp",EDGE,"E242");
            var Q7;
            Q7=sQuery(id+"F7.wireOp",EDGE,"E241");
            var Q8;
            Q8=sQuery(id+"F7.wireOp",EDGE,"E240");
            var Q9;
            Q9=sQuery(id+"F7.wireOp",EDGE,"E239");
            var Q10;
            Q10=sQuery(id+"F7.wireOp",EDGE,"E238");
            var Q11;
            Q11=sQuery(id+"F7.wireOp",EDGE,"E237");
            var Q12;
            Q12=sQuery(id+"F7.wireOp",EDGE,"E236");
            var Q13;
            Q13=sQuery(id+"F7.wireOp",EDGE,"E235");
            var Q14;
            Q14=sQuery(id+"F7.wireOp",EDGE,"E234");
            var Q15;
            Q15=sQuery(id+"F7.wireOp",EDGE,"E233");
            var Q16;
            Q16=sQuery(id+"F7.wireOp",EDGE,"E232");
            var Q17;
            Q17=sQuery(id+"F7.wireOp",EDGE,"E231");
            var Q18;
            Q18=sQuery(id+"F7.wireOp",EDGE,"E230");
            var Q19;
            Q19=sQuery(id+"F7.wireOp",EDGE,"E229");
            var Q20;
            Q20=sQuery(id+"F7.wireOp",EDGE,"E228");
            var Q21;
            Q21=sQuery(id+"F7.wireOp",EDGE,"E227");
            var Q22;
            Q22=sQuery(id+"F7.wireOp",EDGE,"E226");
            var Q23;
            Q23=sQuery(id+"F7.wireOp",EDGE,"E225");
            var Q24;
            Q24=sQuery(id+"F7.wireOp",EDGE,"E224");
            var Q25;
            Q25=sQuery(id+"F7.wireOp",EDGE,"E223");
            var Q26;
            Q26=sQuery(id+"F7.wireOp",EDGE,"E222");
            var Q27;
            Q27=sQuery(id+"F7.wireOp",EDGE,"E221");
            var Q28;
            Q28=sQuery(id+"F7.wireOp",EDGE,"E220");
            var Q29;
            Q29=sQuery(id+"F7.wireOp",EDGE,"E219");
            var Q30;
            Q30=sQuery(id+"F7.wireOp",EDGE,"E218");
            var Q31;
            Q31=sQuery(id+"F7.wireOp",EDGE,"E217");
            var Q32;
            Q32=sQuery(id+"F7.wireOp",EDGE,"E216");
            var Q33;
            Q33=sQuery(id+"F7.wireOp",EDGE,"E215");
            var Q34;
            Q34=sQuery(id+"F7.wireOp",EDGE,"E214");
            var Q35;
            Q35=sQuery(id+"F7.wireOp",EDGE,"E213");
            var Q36;
            Q36=sQuery(id+"F7.wireOp",EDGE,"E212");
            var Q37;
            Q37=sQuery(id+"F7.wireOp",EDGE,"E211");
            var Q38;
            Q38=sQuery(id+"F7.wireOp",EDGE,"E210");
            var Q39;
            Q39=sQuery(id+"F7.wireOp",EDGE,"E209");
            var Q40;
            Q40=sQuery(id+"F7.wireOp",EDGE,"E208");
            var Q41;
            Q41=sQuery(id+"F7.wireOp",EDGE,"E207");
            var Q42;
            Q42=sQuery(id+"F7.wireOp",EDGE,"E211");
            var Q43;
            Q43=sQuery(id+"F7.wireOp",EDGE,"E212");
            var Q44;
            Q44=sQuery(id+"F7.wireOp",EDGE,"E248");
            var Q45;
            Q45=sQuery(id+"F7.wireOp",EDGE,"E249");
            var Q46;
            Q46=sQuery(id+"F7.wireOp",EDGE,"E250");
            var Q47;
            Q47=sQuery(id+"F7.wireOp",EDGE,"E251");
            var Q48;
            Q48=sQuery(id+"F7.wireOp",EDGE,"E252");
            var Q49;
            Q49=sQuery(id+"F7.wireOp",EDGE,"E253");
            var Q50;
            Q50=sQuery(id+"F7.wireOp",EDGE,"E254");
            var Q51;
            Q51=sQuery(id+"F7.wireOp",EDGE,"E255");
            var Q52;
            Q52=sQuery(id+"F7.wireOp",EDGE,"E256");
            var Q53;
            Q53=sQuery(id+"F7.wireOp",EDGE,"E257");
            var Q54;
            Q54=sQuery(id+"F7.wireOp",EDGE,"E258");
            var Q55;
            Q55=sQuery(id+"F7.wireOp",EDGE,"E259");
            var Q56;
            Q56=sQuery(id+"F7.wireOp",EDGE,"E260");
            var Q57;
            Q57=sQuery(id+"F7.wireOp",EDGE,"E261");
            var Q58;
            Q58=sQuery(id+"F7.wireOp",EDGE,"E262");
            var Q59;
            Q59=sQuery(id+"F7.wireOp",EDGE,"E263");
            var Q60;
            Q60=sQuery(id+"F7.wireOp",EDGE,"E264");
            var Q61;
            Q61=sQuery(id+"F7.wireOp",EDGE,"E265");
            var Q62;
            Q62=sQuery(id+"F7.wireOp",EDGE,"E266");
            var Q63;
            Q63=sQuery(id+"F7.wireOp",EDGE,"E267");
            var Q64;
            Q64=sQuery(id+"F7.wireOp",EDGE,"E268");
            var Q65;
            Q65=sQuery(id+"F7.wireOp",EDGE,"E269");
            var Q66;
            Q66=sQuery(id+"F7.wireOp",EDGE,"E270");
            var Q67;
            Q67=sQuery(id+"F7.wireOp",EDGE,"E271");
            var Q68;
            Q68=sQuery(id+"F7.wireOp",EDGE,"E272");
            var Q69;
            Q69=sQuery(id+"F7.wireOp",EDGE,"E273");
            var Q70;
            Q70=sQuery(id+"F7.wireOp",EDGE,"E274");
            var Q71;
            Q71=sQuery(id+"F7.wireOp",EDGE,"E275");
            var Q72;
            Q72=sQuery(id+"F7.wireOp",EDGE,"E276");
            var Q73;
            Q73=sQuery(id+"F7.wireOp",EDGE,"E277");
            var Q74;
            Q74=sQuery(id+"F7.wireOp",EDGE,"E278");
            var Q75;
            Q75=sQuery(id+"F7.wireOp",EDGE,"E279");
            var Q76;
            Q76=sQuery(id+"F7.wireOp",EDGE,"E280");
            var Q77;
            Q77=sQuery(id+"F7.wireOp",EDGE,"E281");
            var Q78;
            Q78=sQuery(id+"F7.wireOp",EDGE,"E282");
            var Q79;
            Q79=sQuery(id+"F7.wireOp",EDGE,"E283");
            var Q80;
            Q80=sQuery(id+"F7.wireOp",EDGE,"E284");
            var Q81;
            Q81=sQuery(id+"F7.wireOp",EDGE,"E285");
            sweep(context, id + "F10", {"operationType" : NewBodyOperationType.ADD, "profiles" : qUnion([Q0]), "path" : qUnion([Q1, Q2, Q3, Q4, Q5, Q6, Q7, Q8, Q9, Q10, Q11, Q12, Q13, Q14, Q15, Q16, Q17, Q18, Q19, Q20, Q21, Q22, Q23, Q24, Q25, Q26, Q27, Q28, Q29, Q30, Q31, Q32, Q33, Q34, Q35, Q36, Q37, Q38, Q39, Q40, Q41, Q42, Q43, Q44, Q45, Q46, Q47, Q48, Q49, Q50, Q51, Q52, Q53, Q54, Q55, Q56, Q57, Q58, Q59, Q60, Q61, Q62, Q63, Q64, Q65, Q66, Q67, Q68, Q69, Q70, Q71, Q72, Q73, Q74, Q75, Q76, Q77, Q78, Q79, Q80, Q81])});
        }
    });
